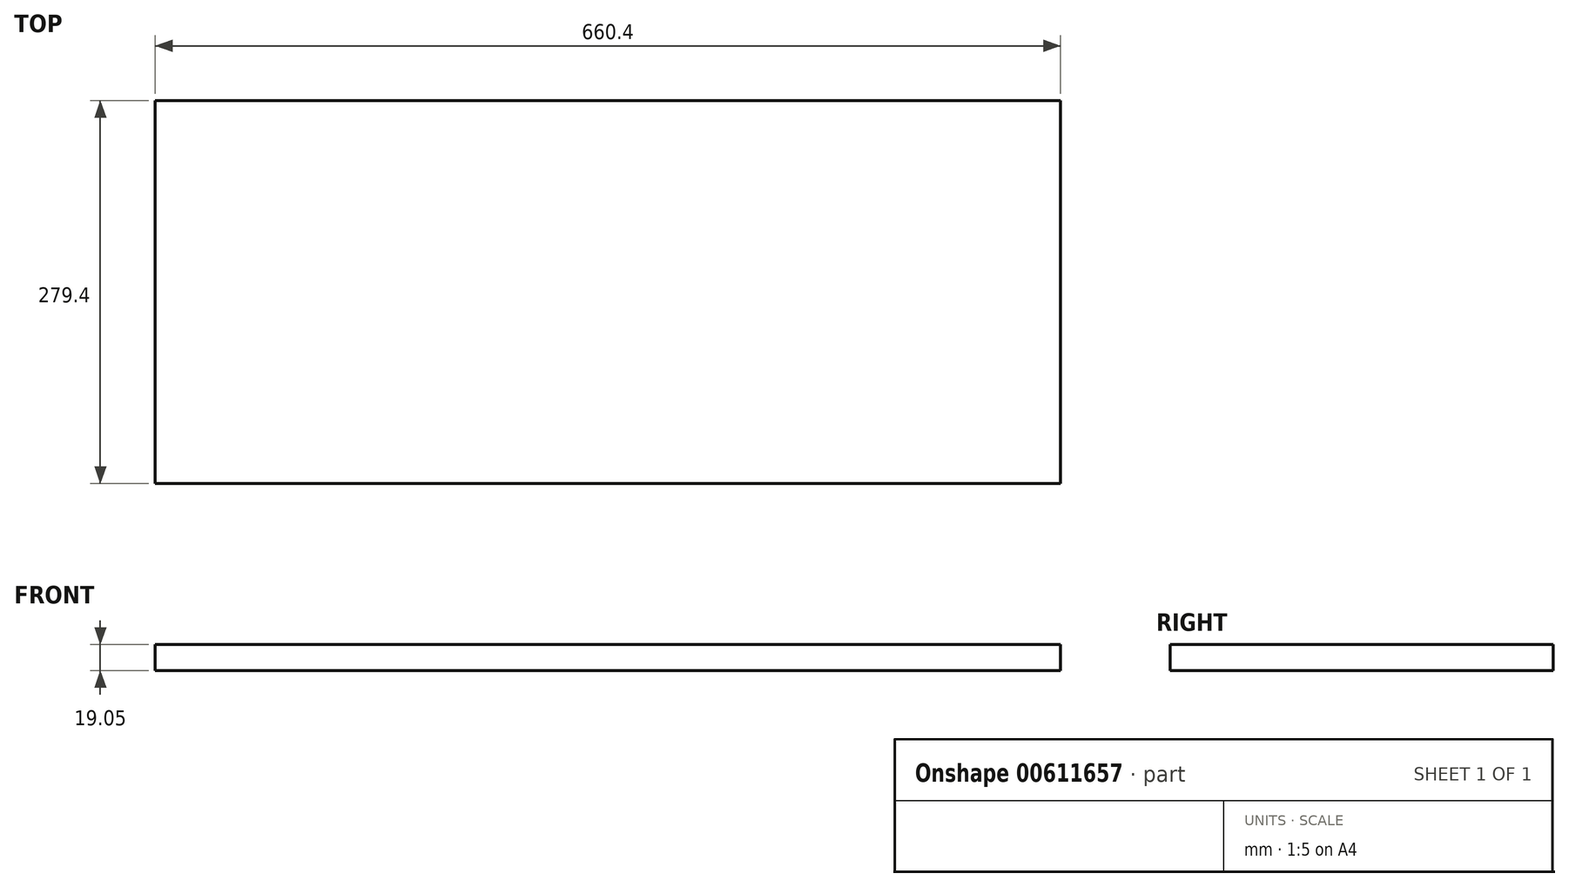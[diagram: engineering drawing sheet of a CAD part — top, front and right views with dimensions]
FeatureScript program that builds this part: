
annotation { "Feature Type Name" : "Feature", "Feature Type Description" : "" }
export const myFeature = defineFeature(function(context is Context, id is Id, definition is map)
    precondition{}
    {
        {
            var Q0;
            Q0=qCreatedBy(makeId("Top.planeOp"),FACE);
            var sketch = newSketch(context, id + "F0", { "sketchPlane" : qUnion([Q0])});
            skLineSegment(sketch, "E0", {"start": v(-332.8, 155.45) * mm, "end": v(327.6, 155.45) * mm});
            skLineSegment(sketch, "E1", {"start": v(327.6, 155.45) * mm, "end": v(327.6, -123.95) * mm});
            skLineSegment(sketch, "E2", {"start": v(327.6, -123.95) * mm, "end": v(-332.8, -123.95) * mm});
            skLineSegment(sketch, "E3", {"start": v(-332.8, -123.95) * mm, "end": v(-332.8, 155.45) * mm});
            skSolve(sketch);
        }
        {
            var Q0;
            Q0=makeQuery(id+"F0.imprint","IMPRINT",FACE,{"disambiguationData":[TD([[makeQuery(id+"F0.imprint","IMPRINT",EDGE,{"derivedFrom":sQuery(id+"F0.wireOp",EDGE,"E0")}),-1.0]])]});
            extrude(context, id + "F1", {"entities" : qUnion([Q0]), "depth" : 19.05 * mm, "offsetDistance" : 25.4 * mm});
        }
    });
